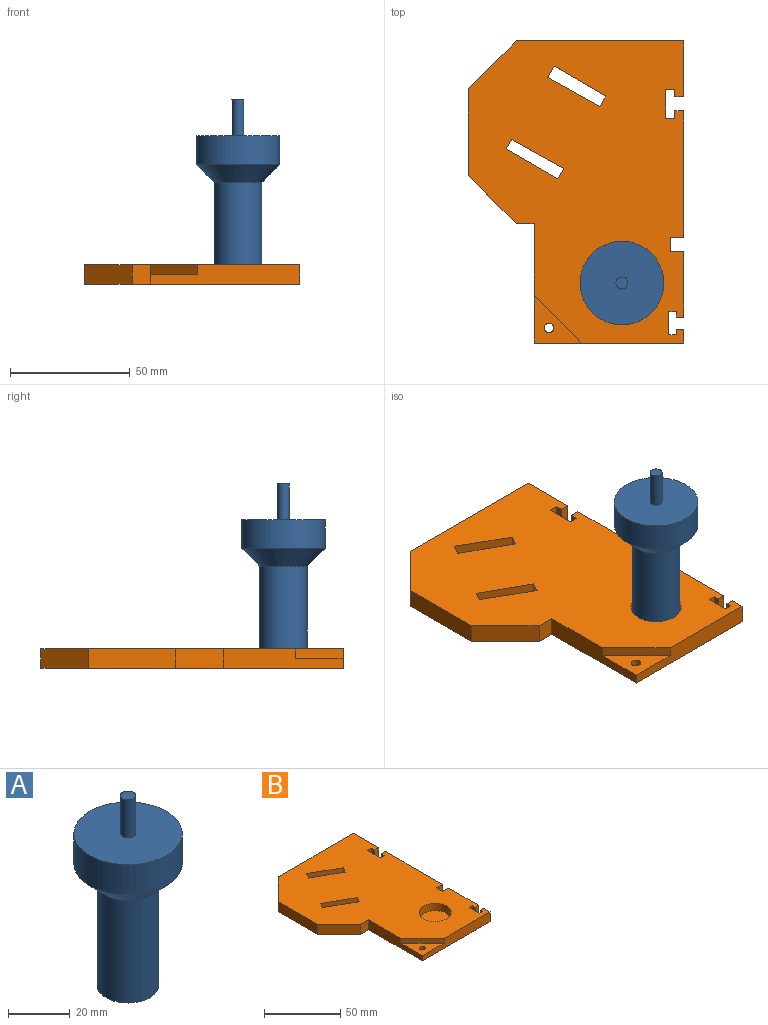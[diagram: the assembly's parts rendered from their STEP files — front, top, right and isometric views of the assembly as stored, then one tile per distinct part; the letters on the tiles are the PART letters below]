
ASSEMBLY  parts=2 mates=1
PART A: 7 faces, bbox 35x35x75 mm
  f0: cylinder r=17.5mm len=35mm, axis (0,0,-1), area 1319.5mm2, adj f1,f5
  f1: plane 35x35mm, normal (0,0,1), area 942.5mm2, adj f0,f3
  f2: cylinder r=10mm len=40.5mm, axis (0,0,-1), area 2544.7mm2, adj f5,f6
  f3: cylinder r=2.5mm len=15mm, axis (0,0,-1), area 235.6mm2, adj f1,f4
  f4: plane 5x5mm, normal (0,0,1), area 19.6mm2, adj f3
  f5: cone r=17.5mm half-angle=45deg, axis (0,0,1), area 916.3mm2, adj f0,f2
  f6: plane 20x20mm, normal (0,0,-1), area 314.2mm2, adj f2
PART B: 43 faces, bbox 90x126.3x8 mm
  f0: plane 21.65x12.5mm, normal (-0.5,-0.87,0), area 200mm2, adj f1,f37,f38,f39
  f1: plane 8x4.33mm, normal (-0.87,0.5,0), area 40mm2, adj f0,f2,f38,f39
  f2: plane 21.84x12.16mm, normal (0.49,0.87,0), area 200mm2, adj f1,f37,f38,f39
  f3: plane 8x4mm, normal (0.87,-0.5,0), area 36.9mm2, adj f4,f35,f38,f39
  f4: plane 21.84x12.17mm, normal (-0.49,-0.87,0), area 200mm2, adj f3,f5,f38,f39
  f5: plane 8x4.33mm, normal (-0.87,0.5,0), area 40mm2, adj f4,f35,f38,f39
  f6: plane 8x7.5mm, normal (0,-1,0), area 60mm2, adj f7,f36,f38,f39
  f7: plane 50x8mm, normal (-1,0,0), area 320mm2, adj f6,f8,f9,f38,f39,f42
  f8: plane 20x20mm, normal (-0.71,-0.71,0), area 113.1mm2, adj f7,f9,f38,f42
  f9: plane 62.5x8mm, normal (0,-1,0), area 420mm2, adj f7,f8,f10,f38,f39,f42
  f10: plane 8x5.84mm, normal (1,0,0), area 46.7mm2, adj f9,f11,f38,f39
  f11: plane 8x3.04mm, normal (0,1,0), area 24.4mm2, adj f10,f12,f38,f39
  f12: plane 8x2.33mm, normal (-1,0.02,0), area 18.6mm2, adj f11,f13,f38,f39
  f13: plane 8x3.08mm, normal (0,1,0), area 24.7mm2, adj f12,f14,f38,f39
  f14: plane 9.63x8mm, normal (1,0,0), area 77mm2, adj f13,f15,f38,f39
  f15: plane 8x3.08mm, normal (0,-1,0), area 24.7mm2, adj f14,f16,f38,f39
  f16: plane 8x2.3mm, normal (-1,-0.02,0), area 18.4mm2, adj f15,f17,f38,f39
  f17: plane 8x3.04mm, normal (0,-1,0), area 24.4mm2, adj f16,f18,f38,f39
  f18: plane 27.49x8mm, normal (1,0,0), area 219.9mm2, adj f17,f19,f38,f39
  f19: plane 8x5.6mm, normal (0,1,0), area 44.8mm2, adj f18,f20,f38,f39
  f20: plane 8x5.64mm, normal (1,0,0), area 45.1mm2, adj f19,f21,f38,f39
  f21: plane 8x5.6mm, normal (0,-1,0), area 44.8mm2, adj f20,f22,f38,f39
  f22: plane 53.11x8mm, normal (1,0,0), area 424.8mm2, adj f21,f23,f38,f39
  f23: plane 8x3.73mm, normal (0,1,0), area 29.8mm2, adj f22,f24,f38,f39
  f24: plane 8x3.08mm, normal (-1,0,0), area 24.7mm2, adj f23,f25,f38,f39
  f25: plane 8x3.77mm, normal (0,1,0), area 30.1mm2, adj f24,f26,f38,f39
  f26: plane 12.03x8mm, normal (1,0,0), area 96.3mm2, adj f25,f27,f38,f39
  f27: plane 8x3.77mm, normal (0,-1,0), area 30.1mm2, adj f26,f28,f38,f39
  f28: plane 8x3.08mm, normal (-1,0,0), area 24.7mm2, adj f27,f29,f38,f39
  f29: plane 8x3.73mm, normal (0,-1,0), area 29.8mm2, adj f28,f30,f38,f39
  f30: plane 23.41x8mm, normal (1,0,0), area 187.3mm2, adj f29,f31,f38,f39
  f31: plane 70x8mm, normal (0,1,0), area 560mm2, adj f30,f32,f38,f39
  f32: plane 20x20mm, normal (-0.71,0.71,0), area 226.3mm2, adj f31,f33,f38,f39
  f33: plane 36.34x8mm, normal (-1,0,0), area 290.7mm2, adj f32,f36,f38,f39
  f34: cylinder r=10.5mm len=21mm, axis (0,0,-1), area 395.8mm2, adj f38,f40
  f35: plane 21.65x12.5mm, normal (0.5,0.87,0), area 200mm2, adj f3,f5,f38,f39
  f36: plane 20x20mm, normal (-0.71,-0.71,0), area 226.3mm2, adj f6,f33,f38,f39
  f37: plane 8x4.67mm, normal (0.87,-0.5,0), area 43.1mm2, adj f0,f2,f38,f39
  f38: plane 126.34x90mm, normal (0,0,1), area 8655.2mm2, adj f0,f1,f2,f3,f4,f5,f6,f7
  f39: plane 126.34x90mm, normal (0,0,-1), area 9189mm2, adj f0,f1,f2,f3,f4,f5,f6,f7
  f40: plane 21x21mm, normal (0,0,1), area 346.4mm2, adj f34
  f41: cylinder r=2mm len=4mm, axis (0,0,-1), area 50.3mm2, adj f39,f42
  f42: plane 20x20mm, normal (0,0,1), area 187.4mm2, adj f7,f8,f9,f41
PLACE A t=(133.34,-138.39,271.49)mm
PLACE B t=(176.65,-113.39,249.49)mm
MATE fastened A.f2 <-> B.f34  axis (0,0,-1) through (133.34,-138.39,251.49)mm
